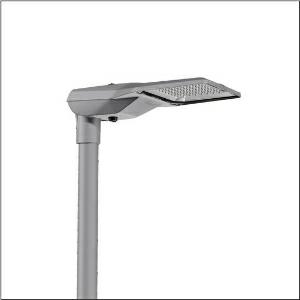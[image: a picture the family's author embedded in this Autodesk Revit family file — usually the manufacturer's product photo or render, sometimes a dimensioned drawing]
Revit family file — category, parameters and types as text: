
# Revit family: streetlight_sl_21_midi___p0_8ab_5xe3r33t08nb_adf9
name_source: partatom
category: Lighting Fixtures
units: mm (PartAtom-declared; Revit-internal decimal feet)

## family parameters
Cut with Voids When Loaded = No
Host = Face
Light Source = No
Part Type = Normal
Room Calculation Point = No
Round Connector Dimension = Use Diameter
Shared = No

## types (1)
- --- (1 x LED, 19710 lm, 151.2 W, 3000K)
    Apparent Load = 151 VA
    CIE Flux Codes = 39 72 97 100 100
    Color Rendering = 70
    Color Temperature = 3000K
    Default Elevation = 1800 mm
    Description = Streetlight SL 21 midi, mast luminaire, primary light control with lens, of PMMA, primary optical cover: cover, of toughened safety glass, transparent, light distribution: P0.8aB, light emission: direct distribution, primary light characteristic: asymmetric, installation type: post-top, side-entry, LED, High Power LED, rated luminous flux: 19.710lm, luminous efficacy: 130lm/W, light colour: 730, colour temperature: 3000K, control gear: D4i, control: pre-setting: logarithmic dimming characteristic, flexible luminous flux parameterisation, time-dependent luminous flux control, constant luminous flux control, overheat protection, mains connection: 230..240V, AC, 50/60Hz, start of lifetime: 151W, end of service life: 157W, reduction: 70W, luminaire housing, of diecast aluminium, powder-coated, Siteco® metallic grey (DB 702S), corrosivity category C5 mid according to DIN EN ISO 12944, multi-level sealing system, sealing non-destructively replaceable, inclination adjustable: 0°, 5°, 10°, 15°, please order mast flange separately, length: 644mm, width: 335mm, height: 110mm, mast flange for spigot size: 42mm (side-entry): 5XC10008XM4, 60/48mm (side-entry/post-top): 5XC10108XM2, 76/60mm (side-entry/post-top): 5XC10108XM1, mounting height: 4..8m, Smart Interface below and above, protection rating (complete): IP66, insulation class (complete): insulation class II (safety insulation), certification: CE, ENEC, ENEC+, VDE, impact resistance: IK10, permissible operating ambient temperature for outdoor applications: -40..+50°C, standard-compliant lighting for roads and squares, packaging unit: 1 piece

Light Distribution: P0.8aB
    Height = 111 mm
    Lamp = 1 x LED
    Lamp Light Flux = 19710 lm
    Lamp Power = 151.2 W
    Lamp count = 1
    Length = 644 mm
    Luminous efficacy = 130 lm/W
    Manufacturer = Siteco
    ModVariant = No
    Model = 5XE3R33T08NB
    Number of Poles = 1
    OnlyDefault = Yes
    Power Factor = 1
    Product Name = Streetlight SL 21 midi | P0.8aB
    Product group = mast luminaire | pylon top
    ProductGroupID = 6100
    Protection Class = Protection class II
    Protection Degree = IP 66
    RLX_Detail_Level = 1
    RLX_Emergency_Light_Flux = 0 lm
    RLX_Emergency_Type = 0
    RLX_Emergency_Type_DB = No
    RlxData = <blob elided: 26685 chars, md5=3f140168>
    Socket = socket
    Standby Power = 0 W
    System Light Flux = 19710 lm
    System Power = 151 W
    Type Comments = factory setting: luminous flux: 100 % | dim-lin: 254 | 802 mA
    Type Image = l_1004304.jpg
    URL = http://relux.com
    VarID = @adj_070904
    Voltage = 0 V
    Weight = 0.00 kg
    Width = 336 mm

## geometry (parser evidence)
native form markers: Blend x4, Sweep x10
no freeform markers — native parametric forms only
